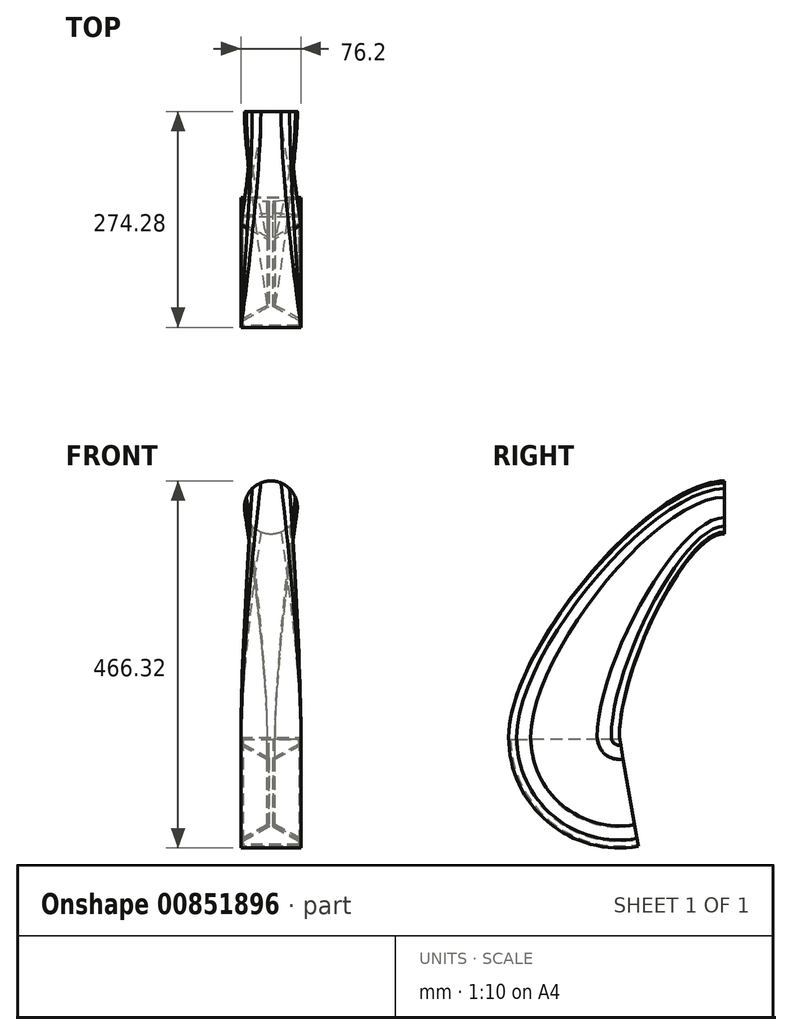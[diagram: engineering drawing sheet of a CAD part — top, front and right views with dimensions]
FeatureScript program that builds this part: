
annotation { "Feature Type Name" : "Feature", "Feature Type Description" : "" }
export const myFeature = defineFeature(function(context is Context, id is Id, definition is map)
    precondition{}
    {
        {
            var Q0;
            Q0=qCreatedBy(makeId("Top.planeOp"),FACE);
            var sketch = newSketch(context, id + "F0", { "sketchPlane" : qUnion([Q0])});
            skLineSegment(sketch, "E0", {"start": v(0, 70.32) * mm, "end": v(-38.1, 70.32) * mm});
            skLineSegment(sketch, "E1", {"start": v(-38.1, 70.32) * mm, "end": v(-38.1, 60.09) * mm});
            skLineSegment(sketch, "E2", {"start": v(-38.1, 60.09) * mm, "end": v(-5.08, 42.24) * mm});
            skLineSegment(sketch, "E3", {"start": v(-5.08, 42.24) * mm, "end": v(-5.08, 0) * mm});
            skLineSegment(sketch, "E4.MirrorCS", {"start": v(0, 70.32) * mm, "end": v(38.1, 70.32) * mm});
            skLineSegment(sketch, "E5.MirrorCS", {"start": v(38.1, 70.32) * mm, "end": v(38.1, 60.09) * mm});
            skLineSegment(sketch, "E6.MirrorCS", {"start": v(38.1, 60.09) * mm, "end": v(5.08, 42.24) * mm});
            skLineSegment(sketch, "E7.MirrorCS", {"start": v(5.08, 42.24) * mm, "end": v(5.08, 0) * mm});
            skLineSegment(sketch, "E8.MirrorCS", {"start": v(-38.1, -60.09) * mm, "end": v(-5.08, -42.24) * mm});
            skLineSegment(sketch, "E9.MirrorCS", {"start": v(-5.08, -42.24) * mm, "end": v(-5.08, 0) * mm});
            skLineSegment(sketch, "E10.MirrorCS", {"start": v(0, -70.32) * mm, "end": v(-38.1, -70.32) * mm});
            skLineSegment(sketch, "E11.MirrorCS", {"start": v(-38.1, -70.32) * mm, "end": v(-38.1, -60.09) * mm});
            skLineSegment(sketch, "E12.MirrorCS", {"start": v(0, -70.32) * mm, "end": v(38.1, -70.32) * mm});
            skLineSegment(sketch, "E13.MirrorCS", {"start": v(38.1, -70.32) * mm, "end": v(38.1, -60.09) * mm});
            skLineSegment(sketch, "E14.MirrorCS", {"start": v(38.1, -60.09) * mm, "end": v(5.08, -42.24) * mm});
            skLineSegment(sketch, "E15.MirrorCS", {"start": v(5.08, -42.24) * mm, "end": v(5.08, 0) * mm});
            skSolve(sketch);
        }
        {
            var Q0;
            Q0=makeQuery(id+"F0.imprint","IMPRINT",FACE,{"disambiguationData":[TD([[makeQuery(id+"F0.imprint","IMPRINT",EDGE,{"derivedFrom":sQuery(id+"F0.wireOp",EDGE,"E0")}),1.0]])]});
            var Q1;
            Q1=sQuery(id+"F0.wireOp",EDGE,"E0");
            revolve(context, id + "F1", {"surfaceOperationType" : NewSurfaceOperationType.NEW, "entities" : qUnion([Q0]), "axis" : qUnion([Q1]), "revolveType" : RevolveType.ONE_DIRECTION, "oppositeDirection" : true, "angle" : 100 * degree});
        }
        {
            var Q0;
            Q0=makeQuery(id+"F1.opRevolve","CAP_FACE",FACE,{"disambiguationData":[OSD([sQuery(id+"F0.wireOp",EDGE,"E0"),sQuery(id+"F0.wireOp",EDGE,"E1"),sQuery(id+"F0.wireOp",EDGE,"E2"),sQuery(id+"F0.wireOp",EDGE,"E3"),sQuery(id+"F0.wireOp",EDGE,"E4.MirrorCS"),sQuery(id+"F0.wireOp",EDGE,"E5.MirrorCS"),sQuery(id+"F0.wireOp",EDGE,"E6.MirrorCS"),sQuery(id+"F0.wireOp",EDGE,"E7.MirrorCS"),sQuery(id+"F0.wireOp",EDGE,"E8.MirrorCS"),sQuery(id+"F0.wireOp",EDGE,"E9.MirrorCS"),sQuery(id+"F0.wireOp",EDGE,"E10.MirrorCS"),sQuery(id+"F0.wireOp",EDGE,"E11.MirrorCS"),sQuery(id+"F0.wireOp",EDGE,"E12.MirrorCS"),sQuery(id+"F0.wireOp",EDGE,"E13.MirrorCS"),sQuery(id+"F0.wireOp",EDGE,"E14.MirrorCS"),sQuery(id+"F0.wireOp",EDGE,"E15.MirrorCS")])],"isStart":false});
            shell(context, id + "F2", {"entities" : qUnion([Q0]), "thickness" : 2.54 * mm});
        }
        {
            var Q0;
            Q0=qCreatedBy(makeId("Front.planeOp"),FACE);
            cPlane(context, id + "F3", {"entities" : qUnion([Q0]), "cplaneType" : CPlaneType.OFFSET, "offset" : 203.96 * mm, "oppositeDirection" : true, "width" : 152.4 * mm, "height" : 152.4 * mm});
        }
        {
            var Q0;
            Q0=qCreatedBy(id+"F3.planeOp",FACE);
            var sketch = newSketch(context, id + "F4", { "sketchPlane" : qUnion([Q0])});
            skCircle(sketch, "E16", {"center": v(0, 292.07) * mm, "radius": 33.6 * mm});
            skSolve(sketch);
        }
        {
            var Q1;
            Q1=makeQuery(id+"F4.imprint","IMPRINT",FACE,{"disambiguationData":[TD([[makeQuery(id+"F4.imprint","IMPRINT",EDGE,{"derivedFrom":sQuery(id+"F4.wireOp",EDGE,"E16")}),1.0]])]});
            var Q2;
            Q2=makeQuery(id+"F0.imprint","IMPRINT",FACE,{"disambiguationData":[TD([[makeQuery(id+"F0.imprint","IMPRINT",EDGE,{"derivedFrom":sQuery(id+"F0.wireOp",EDGE,"E0")}),1.0]])]});
            loft(context, id + "F5", {"operationType" : NewBodyOperationType.ADD, "startCondition" : LoftEndDerivativeType.NORMAL_TO_PROFILE, "startMagnitude" : 1, "endCondition" : LoftEndDerivativeType.NORMAL_TO_PROFILE, "endMagnitude" : 1, "sheetProfilesArray" : [{ "sheetProfileEntities" : qUnion([Q1]) }, { "sheetProfileEntities" : qUnion([Q2]) }]});
        }
    });
